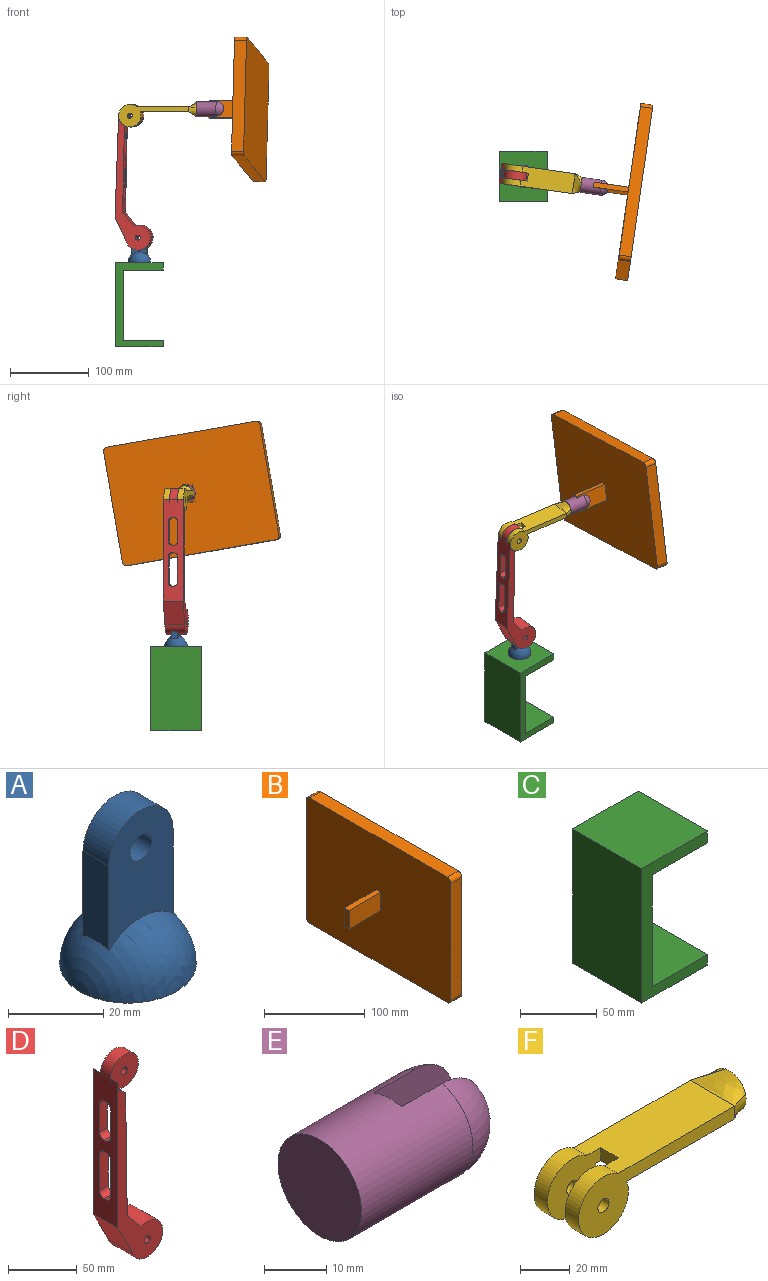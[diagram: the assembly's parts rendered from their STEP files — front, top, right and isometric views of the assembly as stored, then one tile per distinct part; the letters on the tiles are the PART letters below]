
ASSEMBLY  parts=6 mates=5
PART A: 8 faces, bbox 28.6x28.6x41.3 mm
  f0: sphere r=14.29mm, area 1121.3mm2, adj f1,f2,f3,f4,f5
  f1: plane 28.58x28.58mm, normal (0,0,-1), area 641.3mm2, adj f0
  f2: plane 21.81x7.62mm, normal (1,0,0), area 162.6mm2, adj f0,f4,f5,f6
  f3: plane 21.81x7.62mm, normal (-1,0,0), area 162.6mm2, adj f0,f4,f5,f6
  f4: plane 31.33x19.05mm, normal (0,-1,0), area 476.1mm2, adj f0,f2,f3,f6,f7
  f5: plane 31.33x19.05mm, normal (0,1,0), area 476.1mm2, adj f0,f2,f3,f6,f7
  f6: cylinder r=9.53mm len=19.05mm, axis (0,1,0), area 228mm2, adj f2,f3,f4,f5
  f7: cylinder r=3.17mm len=7.62mm, axis (0,1,0), area 152mm2, adj f4,f5
PART B: 15 faces, bbox 59.8x203.2x152.4 mm
  f0: plane 44.45x22.63mm, normal (0,-1,0), area 1006mm2, adj f1,f3,f4,f10
  f1: plane 44.45x6.35mm, normal (0,0,-1), area 282.3mm2, adj f0,f2,f4,f10
  f2: plane 44.45x22.63mm, normal (0,1,0), area 1006mm2, adj f1,f3,f4,f10
  f3: plane 44.45x6.35mm, normal (0,0,1), area 282.3mm2, adj f0,f2,f4,f10
  f4: plane 22.63x6.35mm, normal (-1,0,0), area 143.7mm2, adj f0,f1,f2,f3
  f5: plane 142.24x15.39mm, normal (0,-1,0), area 2189.4mm2, adj f9,f10,f11,f14
  f6: plane 193.04x15.39mm, normal (0,0,-1), area 2971.3mm2, adj f9,f10,f11,f12
  f7: plane 142.24x15.39mm, normal (0,1,0), area 2189.4mm2, adj f9,f10,f12,f13
  f8: plane 193.04x15.39mm, normal (0,0,1), area 2971.3mm2, adj f9,f10,f13,f14
  f9: plane 203.2x152.4mm, normal (1,0,0), area 30945.5mm2, adj f5,f6,f7,f8,f11,f12,f13,f14
  f10: plane 203.2x152.4mm, normal (-1,0,0), area 30801.8mm2, adj f0,f1,f2,f3,f5,f6,f7,f8
  f11: cylinder r=5.08mm len=15.39mm, axis (1,0,0), area 122.8mm2, adj f5,f6,f9,f10
  f12: cylinder r=5.08mm len=15.39mm, axis (-1,0,0), area 122.8mm2, adj f6,f7,f9,f10
  f13: cylinder r=5.08mm len=15.39mm, axis (1,0,0), area 122.8mm2, adj f7,f8,f9,f10
  f14: cylinder r=5.08mm len=15.39mm, axis (-1,0,0), area 122.8mm2, adj f5,f8,f9,f10
PART C: 11 faces, bbox 60.3x63.5x106.8 mm
  f0: plane 63.5x50.8mm, normal (0,0,1), area 3154.5mm2, adj f1,f7,f8,f9,f10
  f1: plane 88.9x63.5mm, normal (1,0,0), area 5645.2mm2, adj f0,f2,f8,f9
  f2: plane 63.5x50.8mm, normal (0,0,-1), area 3225.8mm2, adj f1,f3,f8,f9
  f3: plane 63.5x9.53mm, normal (1,0,0), area 604.8mm2, adj f2,f4,f8,f9
  f4: plane 63.5x60.33mm, normal (0,0,1), area 3830.6mm2, adj f3,f5,f8,f9
  f5: plane 106.78x63.5mm, normal (-1,0,0), area 6780.2mm2, adj f4,f6,f8,f9
  f6: plane 63.5x60.33mm, normal (0,0,-1), area 3759.4mm2, adj f5,f7,f8,f9,f10
  f7: plane 63.5x8.35mm, normal (1,0,0), area 530.3mm2, adj f0,f6,f8,f9
  f8: plane 106.78x60.33mm, normal (0,-1,0), area 1925.1mm2, adj f0,f1,f2,f3,f4,f5,f6,f7
  f9: plane 106.78x60.33mm, normal (0,1,0), area 1925.1mm2, adj f0,f1,f2,f3,f4,f5,f6,f7
  f10: cylinder r=4.76mm len=9.53mm, axis (0,0,-1), area 249.9mm2, adj f0,f6
PART D: 36 faces, bbox 46.1x25.4x184.2 mm
  f0: cylinder r=3.17mm len=10.16mm, axis (0,1,0), area 202.7mm2, adj f17,f19
  f1: cylinder r=14.29mm len=28.58mm, axis (0,1,0), area 751.6mm2, adj f5,f6,f17,f19
  f2: cylinder r=3.17mm len=8.26mm, axis (0,1,0), area 164.7mm2, adj f10,f13
  f3: cylinder r=15.88mm len=31.75mm, axis (0,1,0), area 1606.2mm2, adj f4,f7,f9,f10,f11,f12,f13,f15
  f4: plane 25.4x16.65mm, normal (0.76,0,0.64), area 553mm2, adj f3,f5,f9,f10
  f5: plane 110.14x25.4mm, normal (1,0,0.01), area 1950.5mm2, adj f1,f4,f9,f10,f16,f18,f20,f21
  f6: plane 128.98x25.4mm, normal (-1,0,0), area 2428.9mm2, adj f1,f7,f9,f10,f16,f18,f20,f21
  f7: plane 29.71x25.4mm, normal (-0.89,0,-0.45), area 845.3mm2, adj f3,f6,f9,f10
  f8: cylinder r=3.17mm len=9.53mm, axis (0,1,0), area 190mm2, adj f9,f12
  f9: plane 169.86x46.04mm, normal (0,-1,0), area 2111.6mm2, adj f3,f4,f5,f6,f7,f8,f16
  f10: plane 169.86x46.04mm, normal (0,1,0), area 2111.6mm2, adj f2,f3,f4,f5,f6,f7,f18
  f11: plane 12.7x7.62mm, normal (1,0,0), area 96.8mm2, adj f3,f12,f13,f14
  f12: plane 25.4x25.4mm, normal (0,1,0), area 520.7mm2, adj f3,f8,f11,f14,f15
  f13: plane 25.4x25.4mm, normal (0,-1,0), area 520.7mm2, adj f2,f3,f11,f14,f15
  f14: cylinder r=9.53mm len=9.53mm, axis (0,1,0), area 114mm2, adj f11,f12,f13,f15
  f15: plane 12.7x7.62mm, normal (0,0,-1), area 96.8mm2, adj f3,f12,f13,f14
  f16: cylinder r=14.29mm len=12.77mm, axis (0,-1,0), area 120.3mm2, adj f5,f6,f9,f17
  f17: plane 28.58x28.58mm, normal (0,-1,0), area 609.6mm2, adj f0,f1,f16
  f18: cylinder r=14.29mm len=12.77mm, axis (0,1,0), area 120.3mm2, adj f5,f6,f10,f19
  f19: plane 28.58x28.58mm, normal (0,1,0), area 609.6mm2, adj f0,f1,f18
  f20: plane 32.89x9.26mm, normal (0,-1,0), area 295.3mm2, adj f5,f6,f21,f27
  f21: cylinder r=4.75mm len=8.84mm, axis (1,0,0.01), area 65.1mm2, adj f5,f6,f20,f22
  f22: plane 8.7x1.97mm, normal (0.01,0,-1), area 17.1mm2, adj f5,f6,f21,f23
  f23: cylinder r=4.75mm len=8.84mm, axis (1,0,0.01), area 65.1mm2, adj f5,f6,f22,f24
  f24: plane 32.89x9.26mm, normal (0,1,0), area 295.3mm2, adj f5,f6,f23,f25
  f25: cylinder r=4.75mm len=9.4mm, axis (1,0,0.01), area 69.4mm2, adj f5,f6,f24,f26
  f26: plane 9.33x1.97mm, normal (-0.01,0,1), area 18.3mm2, adj f5,f6,f25,f27
  f27: cylinder r=4.75mm len=9.4mm, axis (1,0,0.01), area 69.4mm2, adj f5,f6,f20,f26
  f28: plane 25.64x8.48mm, normal (0,-1,0), area 211.5mm2, adj f5,f6,f29,f35
  f29: cylinder r=4.75mm len=8.17mm, axis (1,0,0.01), area 60.1mm2, adj f5,f6,f28,f30
  f30: plane 8.03x1.97mm, normal (0.01,0,-1), area 15.8mm2, adj f5,f6,f29,f31
  f31: cylinder r=4.75mm len=8.17mm, axis (1,0,0.01), area 60.1mm2, adj f5,f6,f30,f32
  f32: plane 25.64x8.48mm, normal (0,1,0), area 211.5mm2, adj f5,f6,f31,f33
  f33: cylinder r=4.75mm len=8.62mm, axis (1,0,0.01), area 63.6mm2, adj f5,f6,f32,f34
  f34: plane 8.55x1.97mm, normal (-0.01,0,1), area 16.8mm2, adj f5,f6,f33,f35
  f35: cylinder r=4.75mm len=8.62mm, axis (1,0,0.01), area 63.6mm2, adj f5,f6,f28,f34
PART E: 7 faces, bbox 34.6x19.1x19.1 mm
  f0: sphere r=9.53mm, area 209mm2, adj f1,f6
  f1: cylinder r=9.53mm len=25.4mm, axis (-1,0,0), area 1399.4mm2, adj f0,f2,f3,f4,f5,f6
  f2: plane 19.05x19.05mm, normal (-1,0,0), area 285mm2, adj f1
  f3: sphere r=9.53mm, area 171mm2, adj f1,f5
  f4: plane 19.05x6.35mm, normal (1,0,0), area 118.4mm2, adj f1,f5,f6
  f5: plane 18.03x17.46mm, normal (0,-1,0), area 282mm2, adj f1,f3,f4
  f6: plane 18.48x18.36mm, normal (0,1,0), area 303.1mm2, adj f0,f1,f4
PART F: 16 faces, bbox 98.6x25.4x32.3 mm
  f0: cylinder r=14.22mm len=28.45mm, axis (0,1,0), area 618.5mm2, adj f1,f3,f4,f5
  f1: plane 61.67x25.4mm, normal (0,0,-1), area 1537mm2, adj f0,f4,f5,f6,f8,f9,f10,f13
  f2: cylinder r=3.17mm len=7.62mm, axis (0,1,0), area 152mm2, adj f4,f5
  f3: plane 66.68x25.4mm, normal (0,0,1), area 1613.4mm2, adj f0,f4,f5,f6,f8,f9,f10,f15
  f4: plane 89.1x28.45mm, normal (0,-1,0), area 1008.2mm2, adj f0,f1,f2,f3,f12
  f5: plane 30.32x28.45mm, normal (0,1,0), area 635mm2, adj f0,f1,f2,f3,f10
  f6: cylinder r=14.22mm len=28.45mm, axis (0,-1,0), area 618.5mm2, adj f1,f3,f8,f9
  f7: cylinder r=3.17mm len=7.62mm, axis (0,-1,0), area 152mm2, adj f8,f9
  f8: plane 89.1x28.45mm, normal (0,1,0), area 1008.2mm2, adj f1,f3,f6,f7,f14
  f9: plane 30.32x28.45mm, normal (0,-1,0), area 635mm2, adj f1,f3,f6,f7,f10
  f10: plane 10.16x6.35mm, normal (-1,0,0), area 64.5mm2, adj f1,f3,f5,f9
  f11: plane 19.09x19.09mm, normal (1,0,0), area 285mm2, adj f12,f13,f14,f15
  f12: bspline ~12.42x10.39mm, area 102.5mm2, adj f4,f11,f13,f15
  f13: bspline ~25.4x9.53mm, area 209.3mm2, adj f1,f11,f12,f14
  f14: bspline ~12.42x10.39mm, area 102.5mm2, adj f8,f11,f13,f15
  f15: bspline ~25.4x9.53mm, area 209.3mm2, adj f3,f11,f12,f14
PLACE A rot(axis=(0,0,-1),8.2deg) t=(0.21,2.94,0)mm
PLACE B rot(axis=(-0.77,0.06,-0.64),12.8deg) t=(-2.15,-47.11,4.61)mm
PLACE C at identity fixed
PLACE D rot(axis=(0.02,0.24,-0.97),8.5deg) t=(-4.4,3.61,0.82)mm
PLACE E rot(axis=(-0.77,0.06,-0.64),12.8deg) t=(-1.92,-47.13,4.65)mm
PLACE F rot(axis=(0,0.01,-1),8.2deg) t=(5.18,2.23,0.48)mm
MATE revolute D.f2 <-> A.f6  axis (0.14,0.99,0) through (21.18,3.77,130.18)mm
MATE revolute F.f0 <-> D.f0  axis (-0.14,-0.99,0) through (11.04,5.87,284.63)mm
MATE revolute F.f11 <-> E.f1  axis (0.99,-0.14,0) through (93.87,-11.19,292.93)mm
MATE revolute C.f10 <-> A.f1  axis (0,0,1) through (20.64,0,98.43)mm
MATE fastened E.f5 <-> B.f2  axis (-0.14,-0.98,0.17) through (119.54,-11.09,292.23)mm
